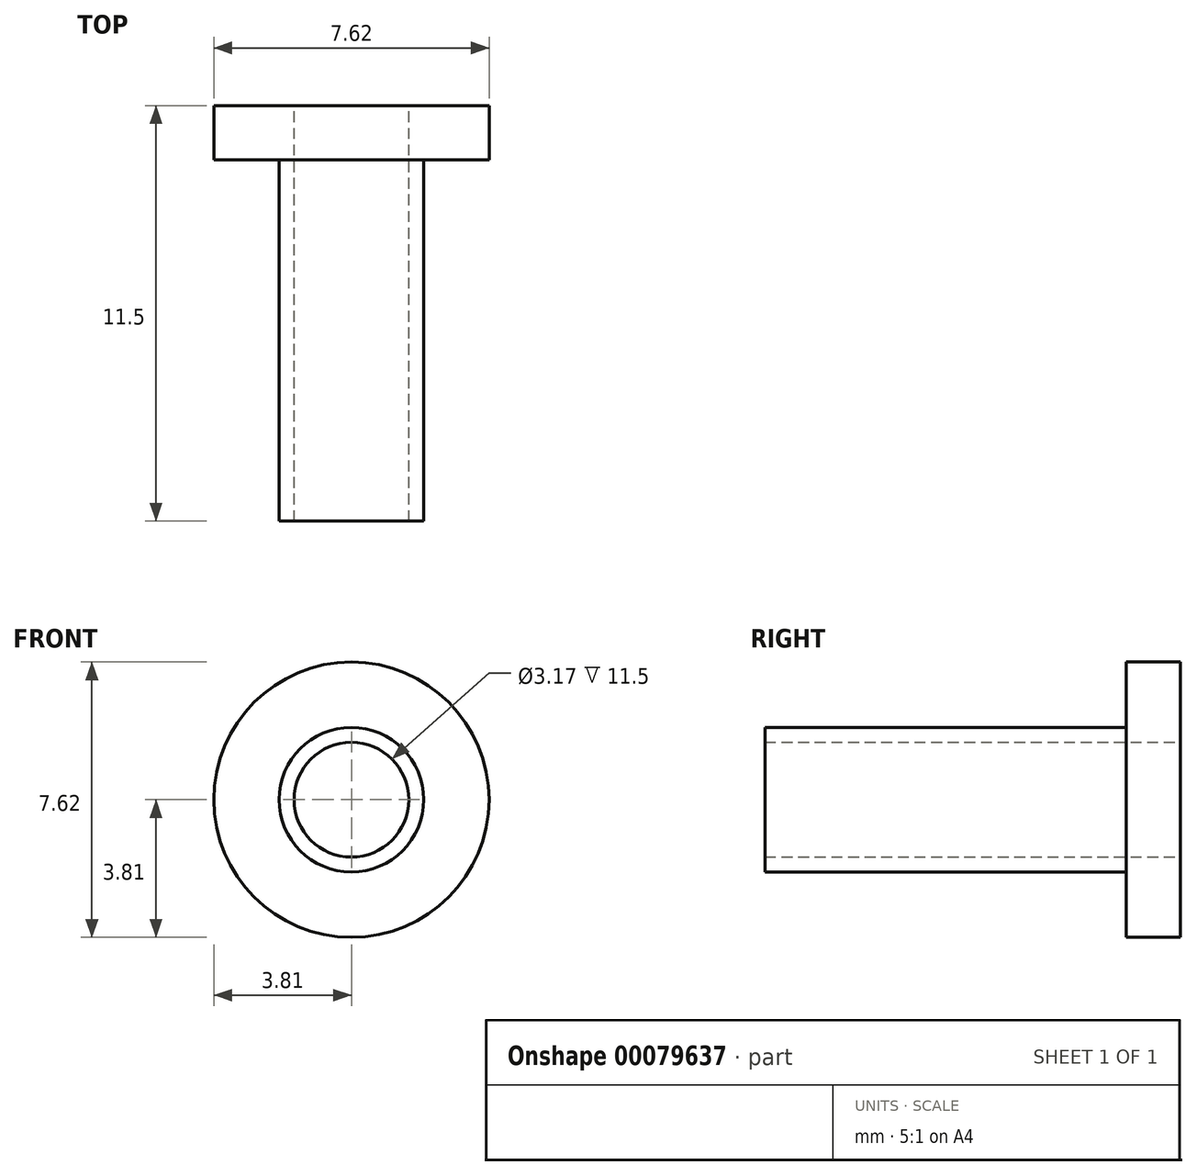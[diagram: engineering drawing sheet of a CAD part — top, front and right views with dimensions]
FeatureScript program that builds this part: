
annotation { "Feature Type Name" : "Feature", "Feature Type Description" : "" }
export const myFeature = defineFeature(function(context is Context, id is Id, definition is map)
    precondition{}
    {
        {
            var Q0;
            Q0=qCreatedBy(makeId("Front.planeOp"),FACE);
            var sketch = newSketch(context, id + "F0", { "sketchPlane" : qUnion([Q0])});
            skCircle(sketch, "E0", {"center": v(0, 0) * mm, "radius": 1.59 * mm});
            skCircle(sketch, "E1", {"center": v(0, 0) * mm, "radius": 3.81 * mm});
            skSolve(sketch);
        }
        {
            var Q0;
            Q0 = qSketchRegion(id + "F0", true);
            extrude(context, id + "F1", {"entities" : qUnion([Q0]), "endBound" : BoundingType.SYMMETRIC, "depth" : 1.5 * mm});
        }
        {
            var Q0;
            Q0=makeQuery(id+"F1.opExtrude","CAP_FACE",FACE,{"disambiguationData":[OSD([sQuery(id+"F0.wireOp",EDGE,"E0"),sQuery(id+"F0.wireOp",EDGE,"E1")])],"isStart":false});
            var sketch = newSketch(context, id + "F2", { "sketchPlane" : qUnion([Q0])});
            skCircle(sketch, "E2", {"center": v(0, 0) * mm, "radius": 2 * mm});
            skSolve(sketch);
        }
        {
            var Q0;
            Q0=makeQuery(id+"F2.imprint","IMPRINT",FACE,{"disambiguationData":[TD([[makeQuery(id+"F2.imprint","IMPRINT",EDGE,{"derivedFrom":sQuery(id+"F2.wireOp",EDGE,"E2")}),1.0]])]});
            extrude(context, id + "F3", {"entities" : qUnion([Q0]), "operationType" : NewBodyOperationType.ADD, "depth" : 10 * mm});
        }
    });
